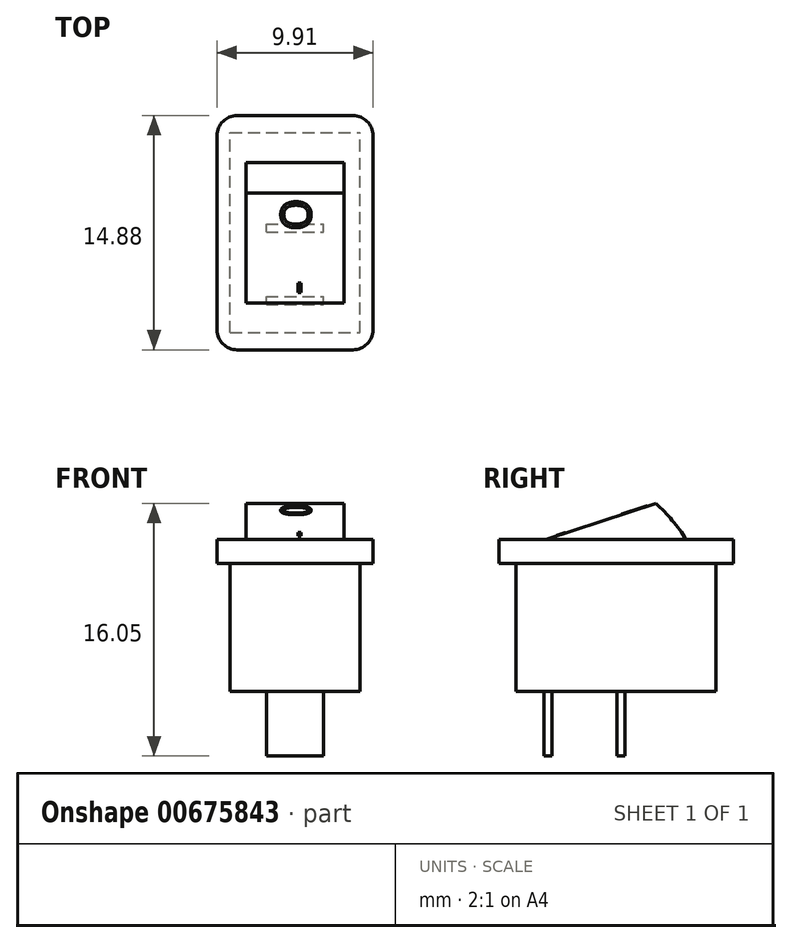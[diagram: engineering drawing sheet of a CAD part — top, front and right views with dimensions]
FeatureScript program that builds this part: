
annotation { "Feature Type Name" : "Feature", "Feature Type Description" : "" }
export const myFeature = defineFeature(function(context is Context, id is Id, definition is map)
    precondition{}
    {
        {
            var Q0;
            Q0=qCreatedBy(makeId("Top.planeOp"),FACE);
            var sketch = newSketch(context, id + "F0", { "sketchPlane" : qUnion([Q0])});
            skLineSegment(sketch, "E0.bottom", {"start": v(0, 0) * mm, "end": v(8.25, 0) * mm});
            skLineSegment(sketch, "E0.top", {"start": v(0, 12.7) * mm, "end": v(8.25, 12.7) * mm});
            skLineSegment(sketch, "E0.left", {"start": v(0, 0) * mm, "end": v(0, 12.7) * mm});
            skLineSegment(sketch, "E0.right", {"start": v(8.26, 0) * mm, "end": v(8.26, 12.7) * mm});
            skSolve(sketch);
        }
        {
            var Q0;
            Q0 = qSketchRegion(id + "F0", true);
            extrude(context, id + "F1", {"entities" : qUnion([Q0]), "depth" : 8.13 * mm, "offsetDistance" : 25.4 * mm});
        }
        {
            var Q0;
            Q0=makeQuery(id+"F1.opExtrude","CAP_FACE",FACE,{"disambiguationData":[OSD([sQuery(id+"F0.wireOp",EDGE,"E0.bottom"),sQuery(id+"F0.wireOp",EDGE,"E0.top"),sQuery(id+"F0.wireOp",EDGE,"E0.left"),sQuery(id+"F0.wireOp",EDGE,"E0.right")])],"isStart":false});
            var sketch = newSketch(context, id + "F2", { "sketchPlane" : qUnion([Q0])});
            skLineSegment(sketch, "E1.bottom", {"start": v(-0.83, 13.8) * mm, "end": v(9.08, 13.8) * mm});
            skLineSegment(sketch, "E1.top", {"start": v(-0.83, -1.1) * mm, "end": v(9.08, -1.1) * mm});
            skLineSegment(sketch, "E1.left", {"start": v(-0.83, 13.8) * mm, "end": v(-0.83, -1.1) * mm});
            skLineSegment(sketch, "E1.right", {"start": v(9.08, 13.8) * mm, "end": v(9.08, -1.1) * mm});
            skLineSegment(sketch, "E2", {"start": v(4.13, 13.8) * mm, "end": v(4.13, 12.7) * mm, "construction": true});
            skLineSegment(sketch, "E3", {"start": v(9.08, 6.35) * mm, "end": v(8.26, 6.35) * mm, "construction": true});
            skSolve(sketch);
        }
        {
            var Q0;
            Q0 = qSketchRegion(id + "F2", true);
            extrude(context, id + "F3", {"entities" : qUnion([Q0]), "operationType" : NewBodyOperationType.ADD, "depth" : 1.52 * mm, "offsetDistance" : 25.4 * mm});
        }
        {
            var Q0;
            Q0=makeQuery(id+"F3.opExtrude","SWEPT_FACE",FACE,{"disambiguationData":[OSD([sQuery(id+"F2.wireOp",EDGE,"E1.right")])]});
            cPlane(context, id + "F4", {"entities" : qUnion([Q0]), "cplaneType" : CPlaneType.OFFSET, "offset" : 1.83 * mm, "oppositeDirection" : true, "width" : 152.4 * mm, "height" : 152.4 * mm});
        }
        {
            var Q0;
            Q0=qCreatedBy(id+"F4.planeOp",FACE);
            var sketch = newSketch(context, id + "F5", { "sketchPlane" : qUnion([Q0])});
            skLineSegment(sketch, "E4", {"start": v(1.9, 9.65) * mm, "end": v(8.88, 11.94) * mm});
            skArc(sketch, "E5", {"start": v(10.8, 9.65) * mm, "mid": v(9.91, 10.85) * mm, "end": v(8.88, 11.94) * mm});
            skLineSegment(sketch, "E6", {"start": v(10.8, 9.65) * mm, "end": v(1.9, 9.65) * mm});
            skSolve(sketch);
        }
        {
            var Q0;
            Q0 = qSketchRegion(id + "F5", true);
            extrude(context, id + "F6", {"entities" : qUnion([Q0]), "operationType" : NewBodyOperationType.ADD, "oppositeDirection" : true, "depth" : 6.22 * mm, "offsetDistance" : 25.4 * mm});
        }
        {
            var Q0;
            Q0=makeQuery(id+"F3.opExtrude","SWEPT_EDGE",EDGE,{"disambiguationData":[OSD([sQuery(id+"F2.wireOp",EDGE,"E1.top"),sQuery(id+"F2.wireOp",EDGE,"E1.right")])]});
            var Q1;
            Q1=makeQuery(id+"F3.opExtrude","SWEPT_EDGE",EDGE,{"disambiguationData":[OSD([sQuery(id+"F2.wireOp",EDGE,"E1.bottom"),sQuery(id+"F2.wireOp",EDGE,"E1.right")])]});
            var Q2;
            Q2=makeQuery(id+"F3.opExtrude","SWEPT_EDGE",EDGE,{"disambiguationData":[OSD([sQuery(id+"F2.wireOp",EDGE,"E1.bottom"),sQuery(id+"F2.wireOp",EDGE,"E1.left")])]});
            var Q3;
            Q3=makeQuery(id+"F3.opExtrude","SWEPT_EDGE",EDGE,{"disambiguationData":[OSD([sQuery(id+"F2.wireOp",EDGE,"E1.top"),sQuery(id+"F2.wireOp",EDGE,"E1.left")])]});
            fillet(context, id + "F7", {"entities" : qUnion([Q0, Q1, Q2, Q3]), "radius" : 1.27 * mm, "tangentPropagation" : true, "allowEdgeOverflow" : false});
        }
        {
            var Q0;
            Q0=makeQuery(id+"F1.opExtrude","CAP_FACE",FACE,{"disambiguationData":[OSD([sQuery(id+"F0.wireOp",EDGE,"E0.bottom"),sQuery(id+"F0.wireOp",EDGE,"E0.top"),sQuery(id+"F0.wireOp",EDGE,"E0.left"),sQuery(id+"F0.wireOp",EDGE,"E0.right")])],"isStart":true});
            var sketch = newSketch(context, id + "F8", { "sketchPlane" : qUnion([Q0])});
            skLineSegment(sketch, "E7.bottom", {"start": v(2.31, -1.78) * mm, "end": v(5.94, -1.78) * mm});
            skLineSegment(sketch, "E7.top", {"start": v(2.31, -2.29) * mm, "end": v(5.94, -2.29) * mm});
            skLineSegment(sketch, "E7.left", {"start": v(2.31, -1.78) * mm, "end": v(2.31, -2.29) * mm});
            skLineSegment(sketch, "E7.right", {"start": v(5.94, -1.78) * mm, "end": v(5.94, -2.29) * mm});
            skLineSegment(sketch, "E8.bottom", {"start": v(2.31, -6.4) * mm, "end": v(5.94, -6.4) * mm});
            skLineSegment(sketch, "E8.top", {"start": v(2.31, -6.9) * mm, "end": v(5.94, -6.9) * mm});
            skLineSegment(sketch, "E8.left", {"start": v(2.31, -6.4) * mm, "end": v(2.31, -6.9) * mm});
            skLineSegment(sketch, "E8.right", {"start": v(5.94, -6.4) * mm, "end": v(5.94, -6.9) * mm});
            skLineSegment(sketch, "E9", {"start": v(4.13, 0) * mm, "end": v(4.13, -1.78) * mm, "construction": true});
            skSolve(sketch);
        }
        {
            var Q0;
            Q0 = qSketchRegion(id + "F8", true);
            extrude(context, id + "F9", {"entities" : qUnion([Q0]), "operationType" : NewBodyOperationType.ADD, "depth" : 4.11 * mm, "offsetDistance" : 25.4 * mm});
        }
        {
            var Q0;
            Q0=makeQuery(id+"F6.opExtrude","SWEPT_FACE",FACE,{"disambiguationData":[OSD([sQuery(id+"F5.wireOp",EDGE,"E4")])]});
            var sketch = newSketch(context, id + "F10", { "sketchPlane" : qUnion([Q0])});
            skText(sketch, "E10", { "text": "-     O", "fontName": "OpenSans-Regular.ttf"});
            const initialGuessF10  = {"E10": [0.00513, 0.00539, 0, 1, 0.0019]};
            skSetInitialGuess(sketch, initialGuessF10);
            skSolve(sketch);
        }
        {
            var Q0;
            Q0 = qSketchRegion(id + "F10", true);
            extrude(context, id + "F11", {"entities" : qUnion([Q0]), "operationType" : NewBodyOperationType.ADD, "depth" : 0.03 * mm, "offsetDistance" : 25.4 * mm});
        }
    });
